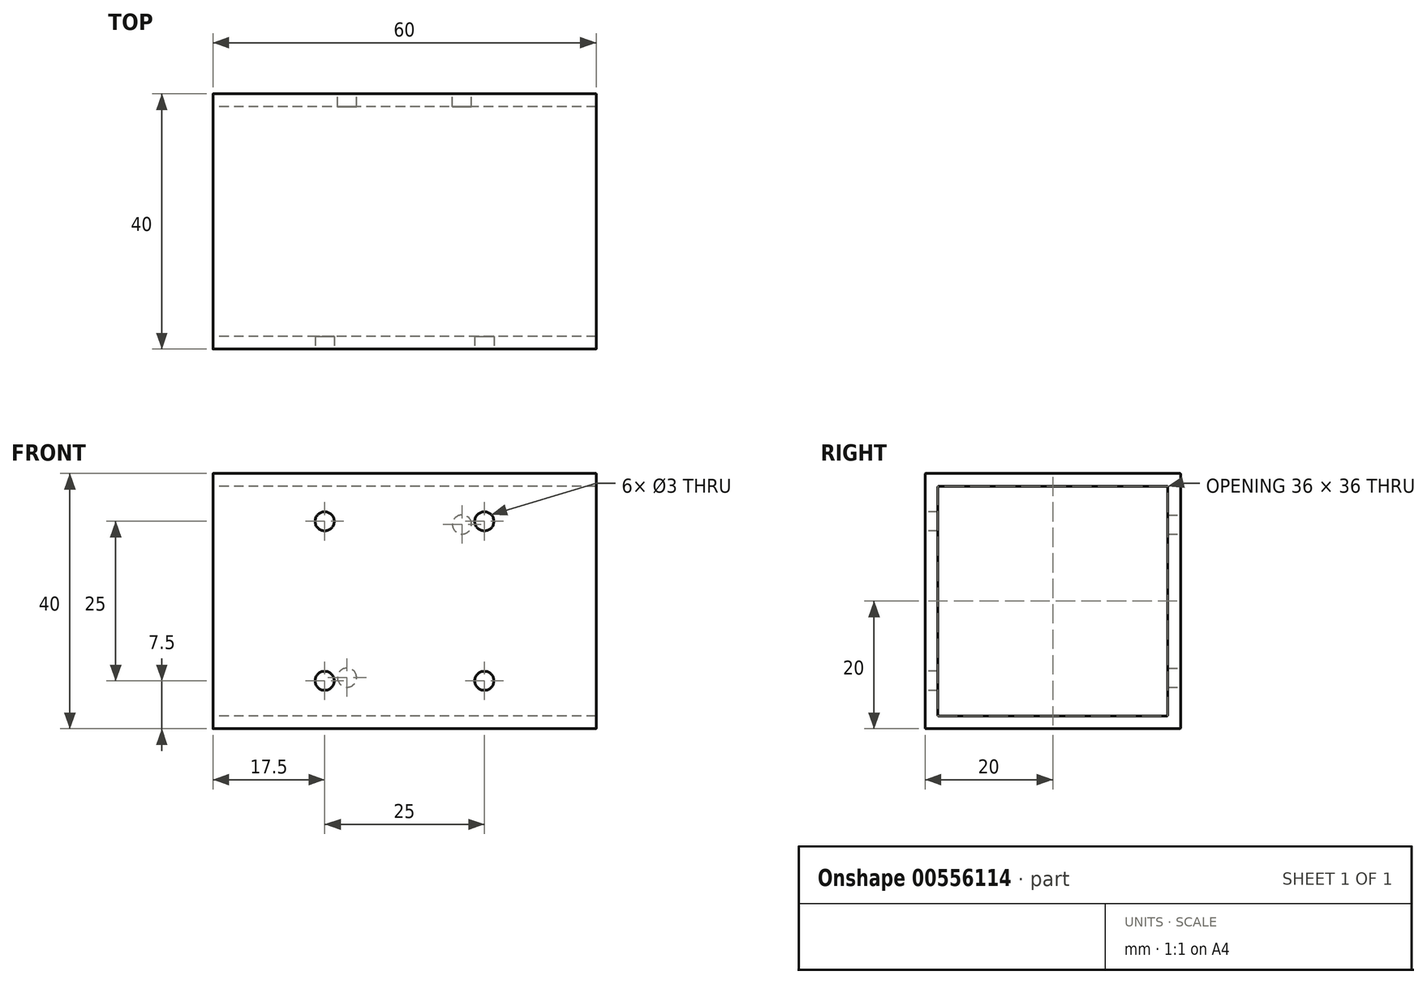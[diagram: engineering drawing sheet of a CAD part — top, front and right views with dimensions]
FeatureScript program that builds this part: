
annotation { "Feature Type Name" : "Feature", "Feature Type Description" : "" }
export const myFeature = defineFeature(function(context is Context, id is Id, definition is map)
    precondition{}
    {
        {
            var Q0;
            Q0=qCreatedBy(makeId("Right.planeOp"),FACE);
            var sketch = newSketch(context, id + "F0", { "sketchPlane" : qUnion([Q0])});
            skLineSegment(sketch, "E0.bottom", {"start": v(20, 20) * mm, "end": v(-20, 20) * mm});
            skLineSegment(sketch, "E0.top", {"start": v(20, -20) * mm, "end": v(-20, -20) * mm});
            skLineSegment(sketch, "E0.left", {"start": v(20, 20) * mm, "end": v(20, -20) * mm});
            skLineSegment(sketch, "E0.right", {"start": v(-20, 20) * mm, "end": v(-20, -20) * mm});
            skPoint(sketch, "E0.middle", {"position": v(0, 0) * mm});
            skSolve(sketch);
        }
        {
            var Q0;
            Q0 = qSketchRegion(id + "F0", true);
            extrude(context, id + "F1", {"entities" : qUnion([Q0]), "depth" : 60 * mm, "offsetDistance" : 25 * mm});
        }
        {
            var Q0;
            Q0=makeQuery(id+"F1.opExtrude","CAP_FACE",FACE,{"disambiguationData":[OSD([sQuery(id+"F0.wireOp",EDGE,"E0.bottom"),sQuery(id+"F0.wireOp",EDGE,"E0.top"),sQuery(id+"F0.wireOp",EDGE,"E0.left"),sQuery(id+"F0.wireOp",EDGE,"E0.right")])],"isStart":false});
            var Q1;
            Q1=makeQuery(id+"F1.opExtrude","CAP_FACE",FACE,{"disambiguationData":[OSD([sQuery(id+"F0.wireOp",EDGE,"E0.bottom"),sQuery(id+"F0.wireOp",EDGE,"E0.top"),sQuery(id+"F0.wireOp",EDGE,"E0.left"),sQuery(id+"F0.wireOp",EDGE,"E0.right")])],"isStart":true});
            shell(context, id + "F2", {"entities" : qUnion([Q0, Q1]), "thickness" : 2 * mm});
        }
        {
            var Q0;
            Q0=makeQuery(id+"F1.opExtrude","SWEPT_FACE",FACE,{"disambiguationData":[OSD([sQuery(id+"F0.wireOp",EDGE,"E0.right")])]});
            var sketch = newSketch(context, id + "F3", { "sketchPlane" : qUnion([Q0])});
            skLineSegment(sketch, "E1", {"start": v(0, -20) * mm, "end": v(60, 20) * mm, "construction": true});
            skLineSegment(sketch, "E2.bottom", {"start": v(42.5, 12.5) * mm, "end": v(17.5, 12.5) * mm});
            skLineSegment(sketch, "E2.top", {"start": v(42.5, -12.5) * mm, "end": v(17.5, -12.5) * mm});
            skLineSegment(sketch, "E2.left", {"start": v(42.5, 12.5) * mm, "end": v(42.5, -12.5) * mm});
            skLineSegment(sketch, "E2.right", {"start": v(17.5, 12.5) * mm, "end": v(17.5, -12.5) * mm});
            skPoint(sketch, "E2.middle", {"position": v(30, 0) * mm});
            skSolve(sketch);
        }
        {
            var Q0;
            Q0=sQuery(id+"F3.wireOp",VERTEX,"E2.right.start");
            var Q1;
            Q1=sQuery(id+"F3.wireOp",VERTEX,"E2.left.start");
            var Q2;
            Q2=sQuery(id+"F3.wireOp",VERTEX,"E2.left.end");
            var Q3;
            Q3=sQuery(id+"F3.wireOp",VERTEX,"E2.right.end");
            var Q4;
            Q4=makeQuery(id+"F1.opExtrude","SWEPT_BODY",BODY,{"disambiguationData":[OSD([sQuery(id+"F0.wireOp",EDGE,"E0.bottom"),sQuery(id+"F0.wireOp",EDGE,"E0.top"),sQuery(id+"F0.wireOp",EDGE,"E0.left"),sQuery(id+"F0.wireOp",EDGE,"E0.right")])]});
            hole(context, id + "F4", {"style" : HoleStyle.SIMPLE, "endStyle" : HoleEndStyle.BLIND, "holeDiameter" : 3 * mm, "majorDiameter" : 5 * mm, "holeDepth" : 2 * mm, "isTappedThrough" : true, "tappedDepth" : 12 * mm, "tapClearance" : 3, "locations" : qUnion([Q0, Q1, Q2, Q3]), "scope" : qUnion([Q4])});
        }
        {
            var Q0;
            Q0=makeQuery(id+"F1.opExtrude","SWEPT_EDGE",EDGE,{"disambiguationData":[OSD([sQuery(id+"F0.wireOp",EDGE,"E0.bottom"),sQuery(id+"F0.wireOp",EDGE,"E0.right")])]});
            var Q1;
            Q1=makeQuery(id+"F1.opExtrude","SWEPT_EDGE",EDGE,{"disambiguationData":[OSD([sQuery(id+"F0.wireOp",EDGE,"E0.bottom"),sQuery(id+"F0.wireOp",EDGE,"E0.left")])]});
            var Q2;
            Q2=makeQuery(id+"F1.opExtrude","SWEPT_EDGE",EDGE,{"disambiguationData":[OSD([sQuery(id+"F0.wireOp",EDGE,"E0.top"),sQuery(id+"F0.wireOp",EDGE,"E0.right")])]});
            var Q3;
            Q3=makeQuery(id+"F1.opExtrude","SWEPT_EDGE",EDGE,{"disambiguationData":[OSD([sQuery(id+"F0.wireOp",EDGE,"E0.top"),sQuery(id+"F0.wireOp",EDGE,"E0.left")])]});
            fillet(context, id + "F5", {"entities" : qUnion([Q0, Q1, Q2, Q3]), "radius" : 0.1 * mm, "tangentPropagation" : true, "allowEdgeOverflow" : false});
        }
        {
            var Q0;
            Q0=makeQuery(id+"F2.opShell","OFFSET_EDGE",EDGE,{"disambiguationData":[OSD([sQuery(id+"F0.wireOp",EDGE,"E0.bottom"),sQuery(id+"F0.wireOp",EDGE,"E0.right")])]});
            var Q1;
            Q1=makeQuery(id+"F2.opShell","OFFSET_EDGE",EDGE,{"disambiguationData":[OSD([sQuery(id+"F0.wireOp",EDGE,"E0.bottom"),sQuery(id+"F0.wireOp",EDGE,"E0.left")])]});
            var Q2;
            Q2=makeQuery(id+"F2.opShell","OFFSET_EDGE",EDGE,{"disambiguationData":[OSD([sQuery(id+"F0.wireOp",EDGE,"E0.top"),sQuery(id+"F0.wireOp",EDGE,"E0.right")])]});
            var Q3;
            Q3=makeQuery(id+"F2.opShell","OFFSET_EDGE",EDGE,{"disambiguationData":[OSD([sQuery(id+"F0.wireOp",EDGE,"E0.top"),sQuery(id+"F0.wireOp",EDGE,"E0.left")])]});
            fillet(context, id + "F6", {"entities" : qUnion([Q0, Q1, Q2, Q3]), "radius" : 0.1 * mm, "tangentPropagation" : true, "allowEdgeOverflow" : false});
        }
        {
            var Q0;
            Q0=makeQuery(id+"F1.opExtrude","SWEPT_FACE",FACE,{"disambiguationData":[OSD([sQuery(id+"F0.wireOp",EDGE,"E0.left")])]});
            var sketch = newSketch(context, id + "F7", { "sketchPlane" : qUnion([Q0])});
            skLineSegment(sketch, "E3", {"start": v(-60, 0) * mm, "end": v(0, 0) * mm, "construction": true});
            skLineSegment(sketch, "E4.bottom", {"start": v(-21, 12) * mm, "end": v(-39, 12) * mm, "construction": true});
            skLineSegment(sketch, "E4.top", {"start": v(-21, -12) * mm, "end": v(-39, -12) * mm, "construction": true});
            skLineSegment(sketch, "E4.left", {"start": v(-21, 12) * mm, "end": v(-21, -12) * mm, "construction": true});
            skLineSegment(sketch, "E4.right", {"start": v(-39, 12) * mm, "end": v(-39, -12) * mm, "construction": true});
            skPoint(sketch, "E4.middle", {"position": v(-30, 0) * mm});
            skSolve(sketch);
        }
        {
            var Q0;
            Q0=sQuery(id+"F7.wireOp",VERTEX,"E4.bottom.end");
            var Q1;
            Q1=sQuery(id+"F7.wireOp",VERTEX,"E4.top.start");
            var Q2;
            Q2=makeQuery(id+"F1.opExtrude","SWEPT_BODY",BODY,{"disambiguationData":[OSD([sQuery(id+"F0.wireOp",EDGE,"E0.bottom"),sQuery(id+"F0.wireOp",EDGE,"E0.top"),sQuery(id+"F0.wireOp",EDGE,"E0.left"),sQuery(id+"F0.wireOp",EDGE,"E0.right")])]});
            hole(context, id + "F8", {"style" : HoleStyle.SIMPLE, "endStyle" : HoleEndStyle.BLIND, "holeDiameter" : 3 * mm, "majorDiameter" : 5 * mm, "holeDepth" : 2 * mm, "isTappedThrough" : true, "tappedDepth" : 12 * mm, "tapClearance" : 3, "startFromSketch" : true, "locations" : qUnion([Q0, Q1]), "scope" : qUnion([Q2])});
        }
    });
